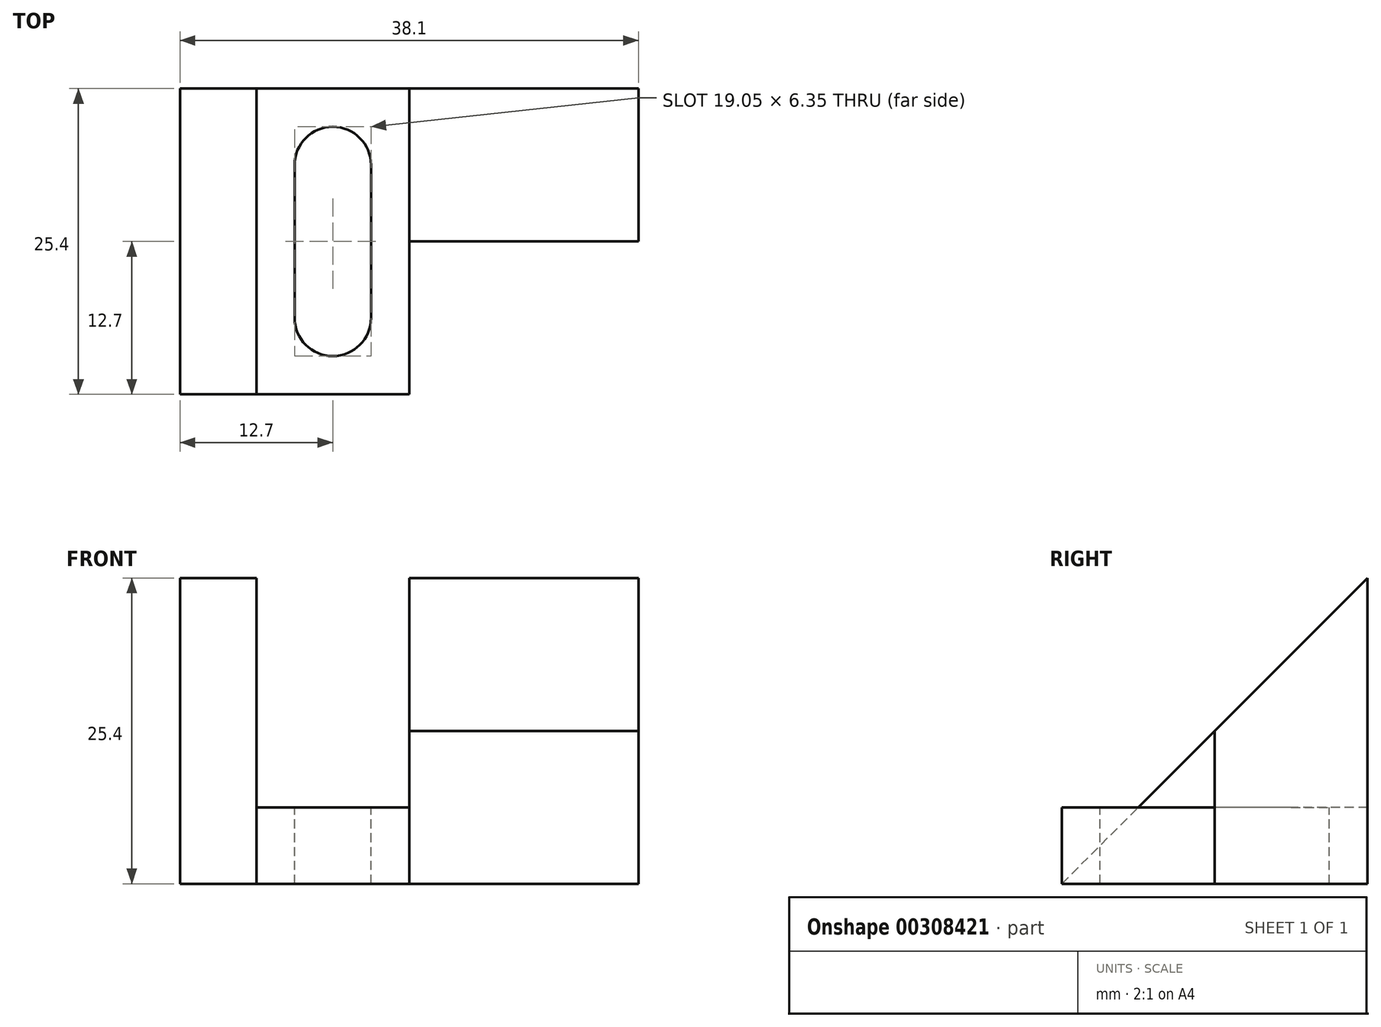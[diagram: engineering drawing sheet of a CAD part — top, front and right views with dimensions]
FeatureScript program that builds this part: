
annotation { "Feature Type Name" : "Feature", "Feature Type Description" : "" }
export const myFeature = defineFeature(function(context is Context, id is Id, definition is map)
    precondition{}
    {
        {
            var Q0;
            Q0=qCreatedBy(makeId("Right.planeOp"),FACE);
            var sketch = newSketch(context, id + "F0", { "sketchPlane" : qUnion([Q0])});
            skLineSegment(sketch, "E0", {"start": v(0, 0) * mm, "end": v(12.7, 0) * mm});
            skLineSegment(sketch, "E1", {"start": v(12.7, 0) * mm, "end": v(12.7, 25.4) * mm});
            skLineSegment(sketch, "E2", {"start": v(12.7, 25.4) * mm, "end": v(0, 12.7) * mm});
            skLineSegment(sketch, "E3", {"start": v(0, 12.7) * mm, "end": v(0, 0) * mm});
            skSolve(sketch);
        }
        {
            var Q0;
            Q0 = qSketchRegion(id + "F0", true);
            extrude(context, id + "F1", {"entities" : qUnion([Q0]), "depth" : 19.05 * mm});
        }
        {
            var Q0;
            Q0=makeQuery(id+"F1.opExtrude","CAP_FACE",FACE,{"disambiguationData":[OSD([sQuery(id+"F0.wireOp",EDGE,"E0"),sQuery(id+"F0.wireOp",EDGE,"E1"),sQuery(id+"F0.wireOp",EDGE,"E2"),sQuery(id+"F0.wireOp",EDGE,"E3")])],"isStart":true});
            var sketch = newSketch(context, id + "F2", { "sketchPlane" : qUnion([Q0])});
            skPoint(sketch, "E4.oppositeSnap0", {"position": v(-6.35, 0) * mm});
            skLineSegment(sketch, "E4.bottom", {"start": v(-12.7, 6.35) * mm, "end": v(12.7, 6.35) * mm});
            skLineSegment(sketch, "E4.top", {"start": v(-12.7, 0) * mm, "end": v(12.7, 0) * mm});
            skLineSegment(sketch, "E4.left", {"start": v(-12.7, 6.35) * mm, "end": v(-12.7, 0) * mm});
            skLineSegment(sketch, "E4.right", {"start": v(12.7, 6.35) * mm, "end": v(12.7, 0) * mm});
            skSolve(sketch);
        }
        {
            var Q0;
            Q0 = qSketchRegion(id + "F2", true);
            extrude(context, id + "F3", {"entities" : qUnion([Q0]), "operationType" : NewBodyOperationType.ADD, "depth" : 12.7 * mm});
        }
        {
            var Q0;
            Q0=makeQuery(id+"F3.opExtrude","CAP_FACE",FACE,{"disambiguationData":[OSD([sQuery(id+"F2.wireOp",EDGE,"E4.bottom"),sQuery(id+"F2.wireOp",EDGE,"E4.top"),sQuery(id+"F2.wireOp",EDGE,"E4.left"),sQuery(id+"F2.wireOp",EDGE,"E4.right")])],"isStart":false});
            var sketch = newSketch(context, id + "F4", { "sketchPlane" : qUnion([Q0])});
            skLineSegment(sketch, "E5", {"start": v(-12.7, 25.4) * mm, "end": v(-12.7, 0) * mm});
            skLineSegment(sketch, "E6", {"start": v(-12.7, 0) * mm, "end": v(12.7, 0) * mm});
            skLineSegment(sketch, "E7", {"start": v(12.7, 0) * mm, "end": v(-12.7, 25.4) * mm});
            skSolve(sketch);
        }
        {
            var Q0;
            Q0 = qSketchRegion(id + "F4", true);
            extrude(context, id + "F5", {"entities" : qUnion([Q0]), "operationType" : NewBodyOperationType.ADD, "depth" : 6.35 * mm});
        }
        {
            var Q0;
            Q0=makeQuery(id+"F3.opExtrude","SWEPT_FACE",FACE,{"disambiguationData":[OSD([sQuery(id+"F2.wireOp",EDGE,"E4.bottom")])]});
            var sketch = newSketch(context, id + "F6", { "sketchPlane" : qUnion([Q0])});
            skArc(sketch, "E8", {"start": v(-3.18, 6.35) * mm, "mid": v(-6.35, 9.52) * mm, "end": v(-9.53, 6.35) * mm});
            skArc(sketch, "E9", {"start": v(-9.52, -6.35) * mm, "mid": v(-6.35, -9.53) * mm, "end": v(-3.17, -6.35) * mm});
            skLineSegment(sketch, "E10", {"start": v(-9.53, 6.35) * mm, "end": v(-9.53, -6.35) * mm});
            skLineSegment(sketch, "E11", {"start": v(-3.18, 6.35) * mm, "end": v(-3.17, -6.35) * mm});
            skSolve(sketch);
        }
        {
            var Q0;
            Q0 = qSketchRegion(id + "F6", true);
            extrude(context, id + "F7", {"entities" : qUnion([Q0]), "operationType" : NewBodyOperationType.REMOVE, "endBound" : BoundingType.THROUGH_ALL, "oppositeDirection" : true, "depth" : 25.4 * mm});
        }
    });
